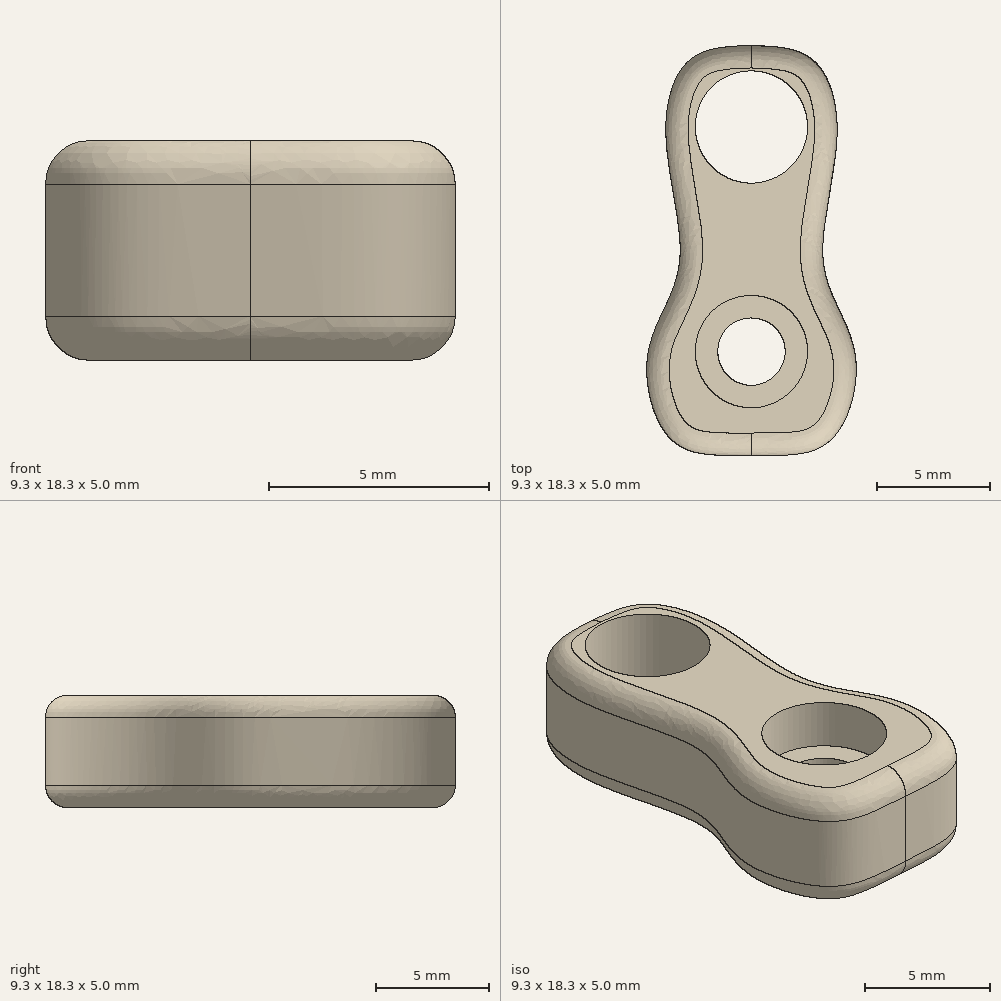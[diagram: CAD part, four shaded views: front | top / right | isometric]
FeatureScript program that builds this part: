
annotation { "Feature Type Name" : "Feature", "Feature Type Description" : "" }
export const myFeature = defineFeature(function(context is Context, id is Id, definition is map)
    precondition{}
    {
        {
            var Q0;
            Q0=qCreatedBy(makeId("Top.planeOp"),FACE);
            var sketch = newSketch(context, id + "F0", { "sketchPlane" : qUnion([Q0])});
            skCircle(sketch, "E0", {"center": v(0, 0) * mm, "radius": 1.5 * mm});
            skCircle(sketch, "E1", {"center": v(0, 0) * mm, "radius": 2.5 * mm});
            skLineSegment(sketch, "E2", {"start": v(0, 10) * mm, "end": v(0, 0) * mm});
            skFitSpline(sketch, "E3", {"points": [v(0, -4.62) * mm, v(-3.62, -3.87) * mm, v(-4.6, 0) * mm, v(-3.23, 3.77) * mm, v(-3.81, 9.64) * mm, v(-2.67, 13.03) * mm, v(0, 13.63) * mm], "startDerivative": vector(-32.66, -0.14) * mm, "endDerivative": vector(21.7, 0.6) * mm});
            skCircle(sketch, "E4", {"center": v(0, 10) * mm, "radius": 2.5 * mm});
            skFitSpline(sketch, "E5.MirrorCS", {"points": [v(0, -4.62) * mm, v(3.62, -3.87) * mm, v(4.6, 0) * mm, v(3.23, 3.77) * mm, v(3.81, 9.64) * mm, v(2.67, 13.03) * mm, v(0, 13.63) * mm], "startDerivative": vector(32.66, -0.14) * mm, "endDerivative": vector(-21.7, 0.6) * mm});
            skSolve(sketch);
        }
        {
            var Q0;
            Q0=makeQuery(id+"F0.imprint","IMPRINT",FACE,{"disambiguationData":[TD([[makeQuery(id+"F0.imprint","IMPRINT",EDGE,{"derivedFrom":sQuery(id+"F0.wireOp",EDGE,"E1")}),-1.0]])]});
            extrude(context, id + "F1", {"entities" : qUnion([Q0]), "depth" : 5 * mm});
        }
        {
            var Q0;
            Q0=makeQuery(id+"F0.imprint","IMPRINT",FACE,{"disambiguationData":[TD([[makeQuery(id+"F0.imprint","IMPRINT",EDGE,{"derivedFrom":sQuery(id+"F0.wireOp",EDGE,"E0")}),-1.0]])]});
            extrude(context, id + "F2", {"entities" : qUnion([Q0]), "operationType" : NewBodyOperationType.ADD, "depth" : 3 * mm});
        }
        {
            var Q0;
            Q0=makeQuery(id+"F1.opExtrude","CAP_EDGE",EDGE,{"disambiguationData":[OSD([sQuery(id+"F0.wireOp",EDGE,"E5.MirrorCS")])],"isStart":false});
            var Q1;
            Q1=makeQuery(id+"F1.opExtrude","CAP_EDGE",EDGE,{"disambiguationData":[OSD([sQuery(id+"F0.wireOp",EDGE,"E5.MirrorCS")])],"isStart":true});
            fillet(context, id + "F3", {"entities" : qUnion([Q0, Q1]), "radius" : 1 * mm, "tangentPropagation" : true, "allowEdgeOverflow" : false});
        }
    });
